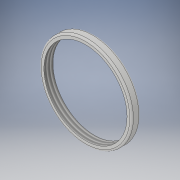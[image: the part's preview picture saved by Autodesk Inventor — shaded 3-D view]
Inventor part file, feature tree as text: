
AUTODESK INVENTOR PART (.ipt)
format: ipt  version: 2019 (Build 230136000, 136)  size: 125,440 bytes
history: native  units: mm
features: extrude x1, thread x1, fillet x1, sketch x1
ambient origin geometry x8: Origin, YZ Plane, XZ Plane, XY Plane, X Axis, Y Axis, Z Axis, Center Point
bodies: Solid1 (feature_tree)
feature tree (4):
  extrude  "Extrusion1"  Depth=2.0mm
  thread  "Thread1"  [1 undecoded]
  fillet  "Fillet1"  Radius=10.0mm
  sketch  "Sketch1"  dims[d0=92.0mm d1=102.0mm d2=10.0mm d3=0.0mm d4=10.0mm d5=0.0mm d6=2.0mm]
note: 1 required parameter value undecoded (feature->parameter linkage not recoverable at this tier; creation-order binding heuristic only, values carry confidence <= 0.55)
